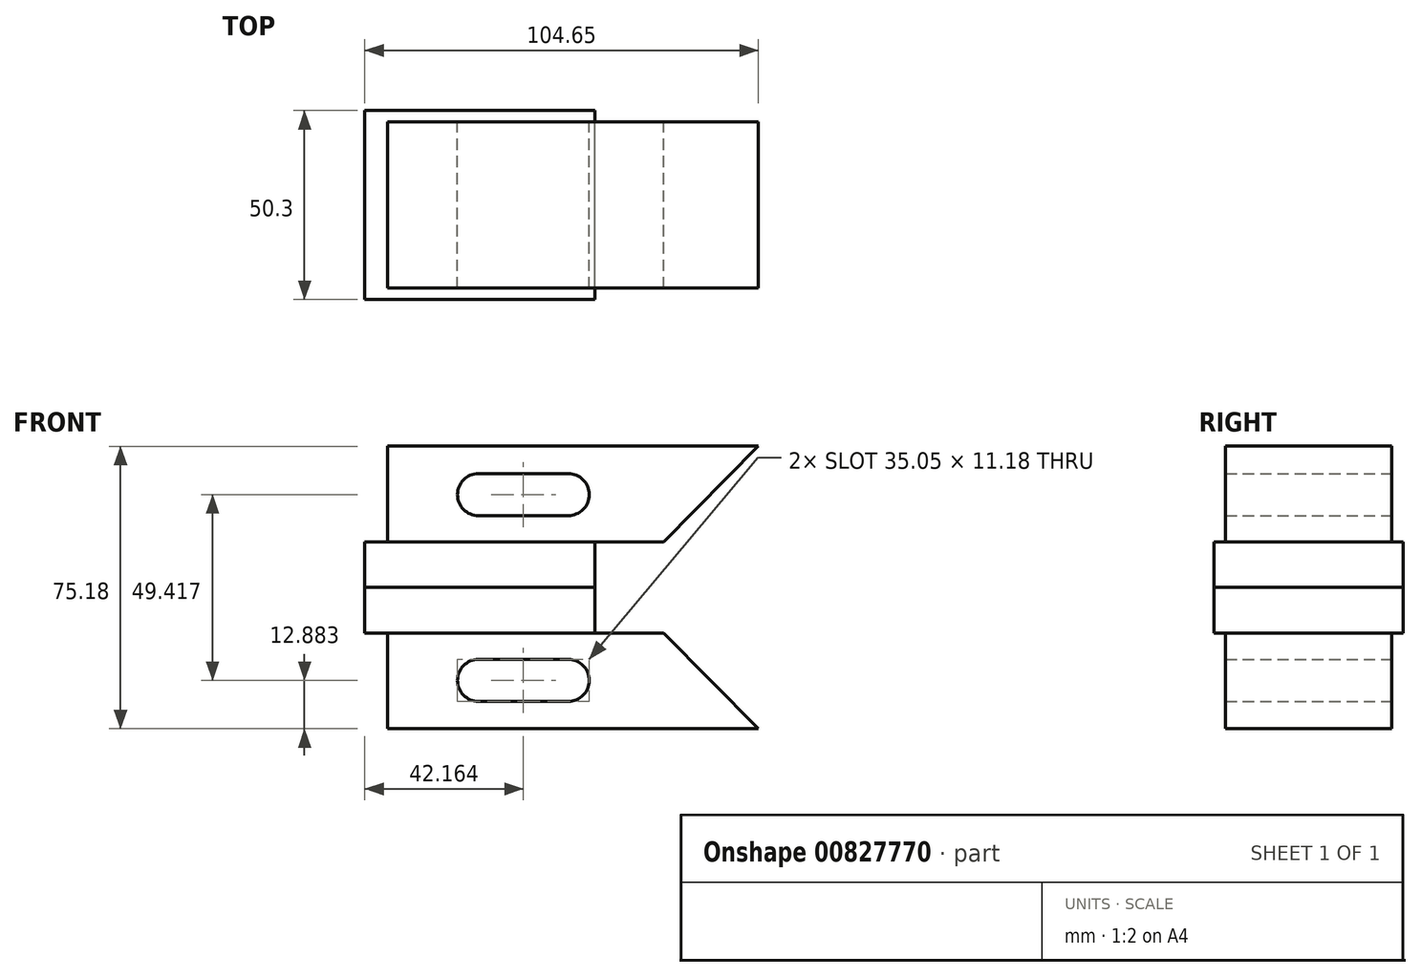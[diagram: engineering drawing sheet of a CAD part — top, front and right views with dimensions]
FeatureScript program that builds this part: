
annotation { "Feature Type Name" : "Feature", "Feature Type Description" : "" }
export const myFeature = defineFeature(function(context is Context, id is Id, definition is map)
    precondition{}
    {
        {
            var Q0;
            Q0=qCreatedBy(makeId("Front.planeOp"),FACE);
            var sketch = newSketch(context, id + "F0", { "sketchPlane" : qUnion([Q0])});
            skLineSegment(sketch, "E0.bottom", {"start": v(0, 0) * mm, "end": v(66.1, 0) * mm});
            skLineSegment(sketch, "E0.top", {"start": v(0, 25.44) * mm, "end": v(86.57, 25.44) * mm});
            skLineSegment(sketch, "E0.left", {"start": v(0, 0) * mm, "end": v(0, 25.44) * mm});
            skLineSegment(sketch, "E1.bottom", {"start": v(0, 25.44) * mm, "end": v(6.1, 25.44) * mm});
            skLineSegment(sketch, "E1.top", {"start": v(0, 0) * mm, "end": v(6.1, 0) * mm});
            skLineSegment(sketch, "E1.left", {"start": v(0, 25.44) * mm, "end": v(0, 0) * mm});
            skLineSegment(sketch, "E1.right", {"start": v(6.1, 25.44) * mm, "end": v(6.1, 0) * mm});
            skCircle(sketch, "E2", {"center": v(30.23, 12.56) * mm, "radius": 5.59 * mm});
            skPoint(sketch, "E3.orphan", {"position": v(6.1, 12.72) * mm});
            skCircle(sketch, "E4", {"center": v(54.1, 12.56) * mm, "radius": 5.59 * mm});
            skLineSegment(sketch, "E5", {"start": v(30.23, 18.15) * mm, "end": v(54.1, 18.15) * mm});
            skLineSegment(sketch, "E6", {"start": v(30.23, 6.97) * mm, "end": v(54.1, 6.97) * mm});
            skLineSegment(sketch, "E7", {"start": v(86.57, 25.44) * mm, "end": v(104.65, 25.44) * mm});
            skLineSegment(sketch, "E8.bottom", {"start": v(0, 0) * mm, "end": v(61.15, 0) * mm});
            skLineSegment(sketch, "E8.top", {"start": v(0, -12.15) * mm, "end": v(61.15, -12.15) * mm});
            skLineSegment(sketch, "E8.left", {"start": v(0, 0) * mm, "end": v(0, -12.15) * mm});
            skLineSegment(sketch, "E8.right", {"start": v(61.15, 0) * mm, "end": v(61.15, -12.15) * mm});
            skLineSegment(sketch, "E9", {"start": v(69.6, 7.92) * mm, "end": v(69.6, 25.44) * mm});
            skLineSegment(sketch, "E10", {"start": v(104.65, 25.44) * mm, "end": v(79.51, 0) * mm});
            skLineSegment(sketch, "E11", {"start": v(79.51, 0) * mm, "end": v(66.1, 0) * mm});
            skSolve(sketch);
        }
        {
            var Q0;
            {var subQ3=sQuery(id+"F0.wireOp",EDGE,"E1.right");Q0=makeQuery(id+"F0.imprint","IMPRINT",FACE,{"disambiguationData":[TD([[makeQuery(id+"F0.imprint","IMPRINT",EDGE,{"derivedFrom":subQ3}),1.0]])]});}
            var Q1;
            Q1=makeQuery(id+"F0.imprint","IMPRINT",FACE,{"disambiguationData":[TD([[makeQuery(id+"F0.imprint","IMPRINT",EDGE,{"derivedFrom":sQuery(id+"F0.wireOp",EDGE,"E1.bottom")}),-1.0]])]});
            extrude(context, id + "F1", {"entities" : qUnion([Q0, Q1]), "endBound" : BoundingType.SYMMETRIC, "depth" : 25.4 * mm, "offsetDistance" : 25.4 * mm});
        }
        {
            var Q0;
            {var subQ2=sQuery(id+"F0.wireOp",EDGE,"E7");Q0=makeQuery(id+"F0.imprint","IMPRINT",FACE,{"disambiguationData":[TD([[makeQuery(id+"F0.imprint","IMPRINT",EDGE,{"derivedFrom":subQ2}),-1.0]])]});}
            extrude(context, id + "F2", {"entities" : qUnion([Q0]), "operationType" : NewBodyOperationType.ADD, "endBound" : BoundingType.SYMMETRIC, "depth" : 44.2 * mm, "offsetDistance" : 25.4 * mm});
        }
        {
            var Q0;
            {var subQ1=sQuery(id+"F0.wireOp",EDGE,"E8.left");Q0=makeQuery(id+"F0.imprint","IMPRINT",FACE,{"disambiguationData":[TD([[makeQuery(id+"F0.imprint","IMPRINT",EDGE,{"derivedFrom":subQ1}),1.0]])]});}
            extrude(context, id + "F3", {"entities" : qUnion([Q0]), "operationType" : NewBodyOperationType.ADD, "endBound" : BoundingType.SYMMETRIC, "depth" : 50.3 * mm, "offsetDistance" : 25.4 * mm});
        }
        {
            var Q0;
            Q0=makeQuery(id+"F1.opExtrude","SWEPT_BODY",BODY,{"disambiguationData":[OSD([sQuery(id+"F0.wireOp",EDGE,"E0.bottom"),sQuery(id+"F0.wireOp",EDGE,"E0.top"),sQuery(id+"F0.wireOp",EDGE,"E1.bottom"),sQuery(id+"F0.wireOp",EDGE,"E1.left"),sQuery(id+"F0.wireOp",EDGE,"E2"),sQuery(id+"F0.wireOp",EDGE,"E4"),sQuery(id+"F0.wireOp",EDGE,"E5"),sQuery(id+"F0.wireOp",EDGE,"E6"),sQuery(id+"F0.wireOp",EDGE,"YIVdZXHk-qXrA-38Pr-xLbY-mIIrmAXwhGj4"),sQuery(id+"F0.wireOp",EDGE,"E8.bottom"),sQuery(id+"F0.wireOp",EDGE,"VULu4nDQ-gV5e-28EC-K1EO-OLVXIcdKoPQr"),sQuery(id+"F0.wireOp",EDGE,"E9")])]});
            var Q1;
            Q1=makeQuery(id+"F3.opExtrude","SWEPT_FACE",FACE,{"disambiguationData":[OSD([sQuery(id+"F0.wireOp",EDGE,"E8.top")])]});
            mirror(context, id + "F4", {"entities" : qUnion([Q0]), "mirrorPlane" : qUnion([Q1])});
        }
    });
